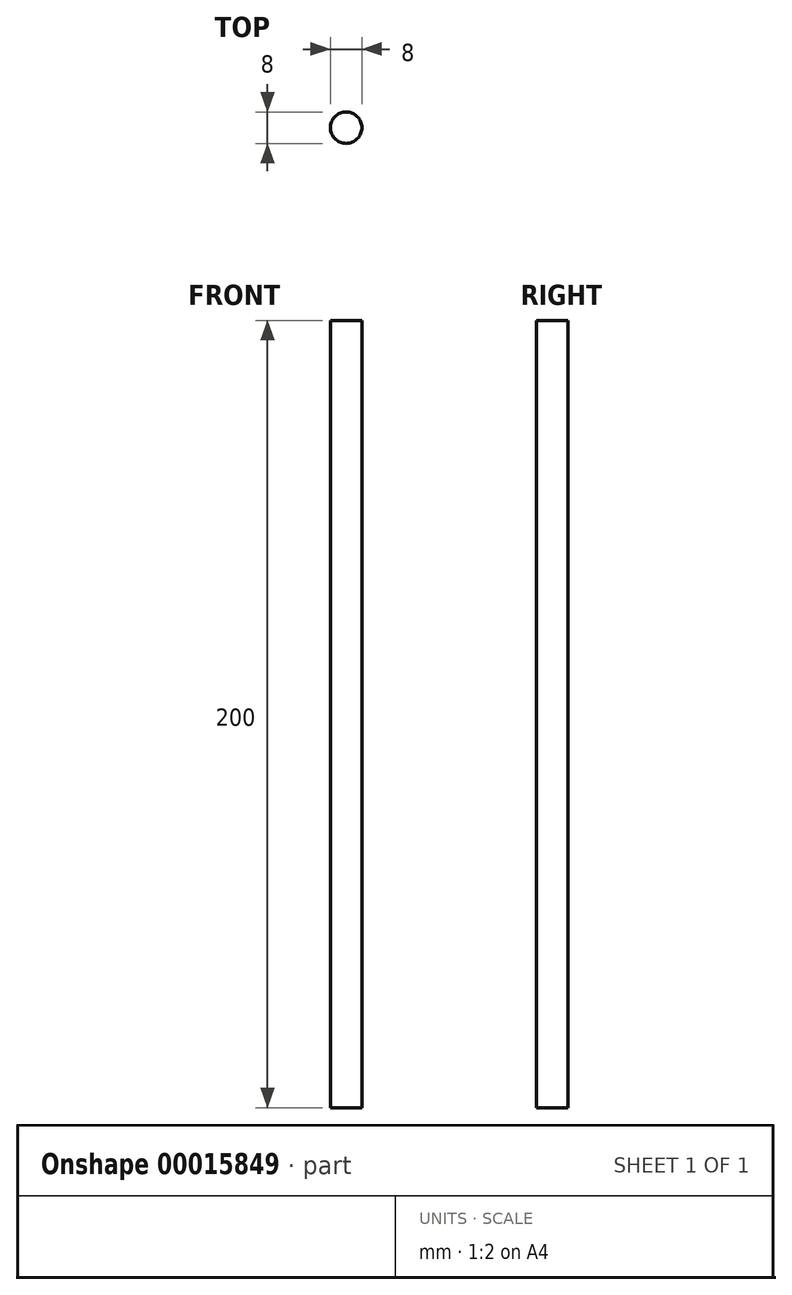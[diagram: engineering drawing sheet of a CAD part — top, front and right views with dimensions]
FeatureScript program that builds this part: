
annotation { "Feature Type Name" : "Feature", "Feature Type Description" : "" }
export const myFeature = defineFeature(function(context is Context, id is Id, definition is map)
    precondition{}
    {
        {
            var Q0;
            Q0=qCreatedBy(makeId("Top.planeOp"),FACE);
            var sketch = newSketch(context, id + "F0", { "sketchPlane" : qUnion([Q0])});
            skCircle(sketch, "E0", {"center": v(0, 0) * mm, "radius": 4 * mm});
            skSolve(sketch);
        }
        {
            var Q0;
            Q0 = qSketchRegion(id + "F0", true);
            extrude(context, id + "F1", {"entities" : qUnion([Q0]), "depth" : 200 * mm});
        }
    });
